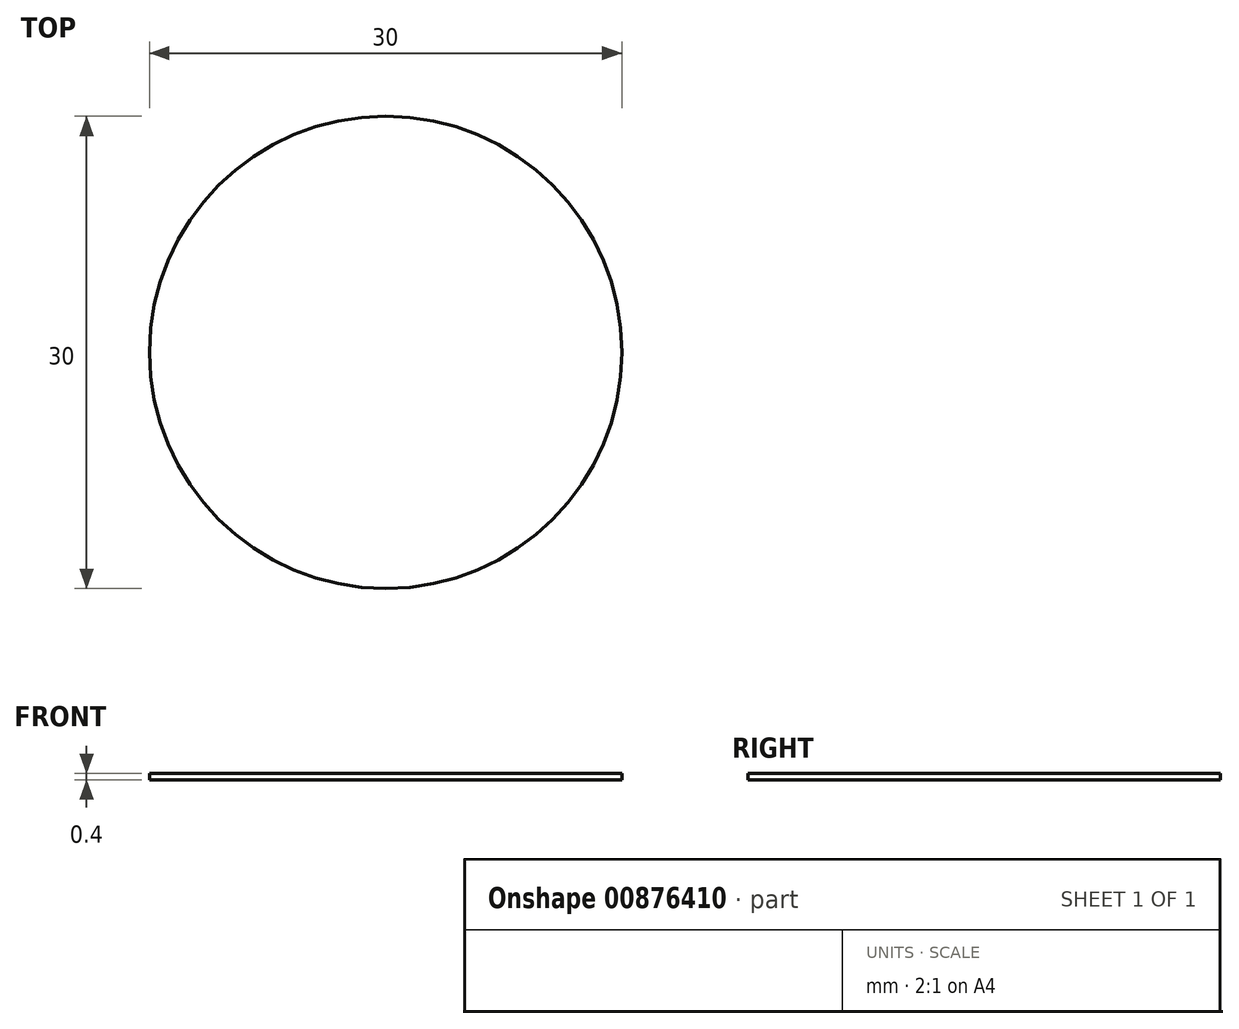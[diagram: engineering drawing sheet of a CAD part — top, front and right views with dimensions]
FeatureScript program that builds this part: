
annotation { "Feature Type Name" : "Feature", "Feature Type Description" : "" }
export const myFeature = defineFeature(function(context is Context, id is Id, definition is map)
    precondition{}
    {
        {
            var Q0;
            Q0=qCreatedBy(makeId("Top.planeOp"),FACE);
            var sketch = newSketch(context, id + "F0", { "sketchPlane" : qUnion([Q0])});
            skCircle(sketch, "E0", {"center": v(0, 0) * mm, "radius": 15 * mm});
            skSolve(sketch);
        }
        {
            var Q0;
            Q0=makeQuery(id+"F0.imprint","IMPRINT",FACE,{"disambiguationData":[TD([[makeQuery(id+"F0.imprint","IMPRINT",EDGE,{"derivedFrom":sQuery(id+"F0.wireOp",EDGE,"E0")}),1.0]])]});
            extrude(context, id + "F1", {"entities" : qUnion([Q0]), "depth" : 0.4 * mm, "offsetDistance" : 25 * mm});
        }
    });
